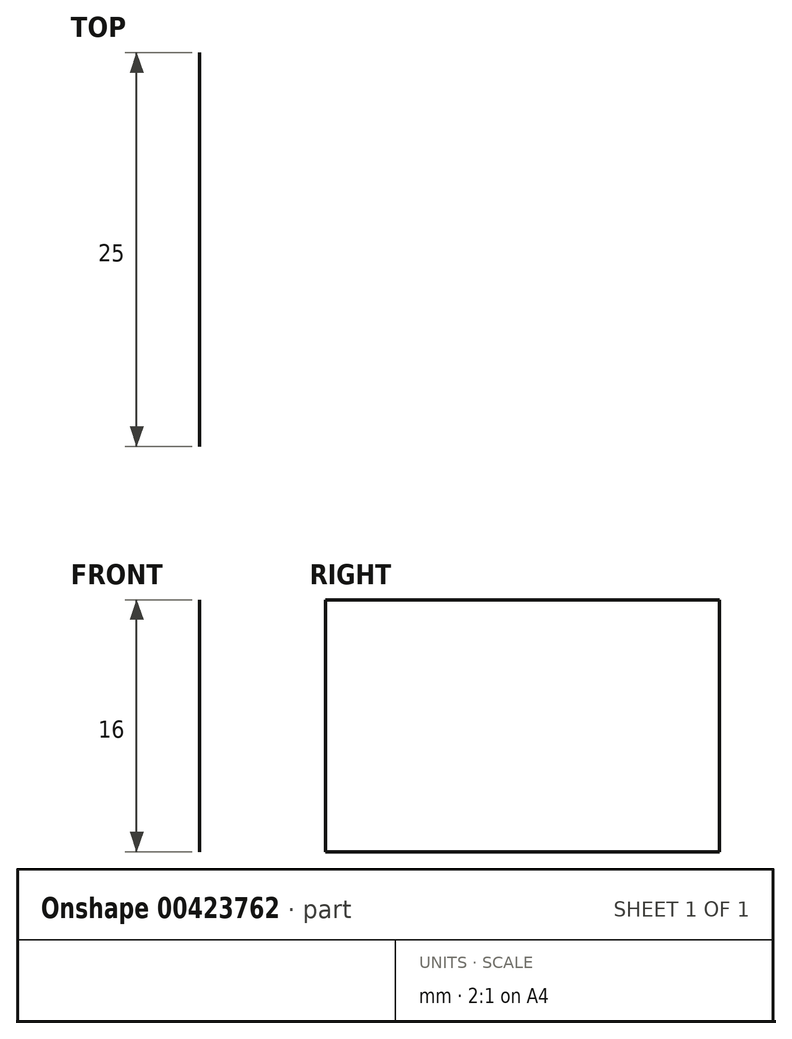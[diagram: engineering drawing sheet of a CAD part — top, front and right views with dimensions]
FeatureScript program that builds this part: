
annotation { "Feature Type Name" : "Feature", "Feature Type Description" : "" }
export const myFeature = defineFeature(function(context is Context, id is Id, definition is map)
    precondition{}
    {
        {
            var Q0;
            Q0=qCreatedBy(makeId("Front.planeOp"),FACE);
            var sketch = newSketch(context, id + "F0", { "sketchPlane" : qUnion([Q0])});
            skLineSegment(sketch, "E0", {"start": v(0, 0) * mm, "end": v(16, 0) * mm});
            skLineSegment(sketch, "E1", {"start": v(-16, 0) * mm, "end": v(0, 0) * mm});
            skLineSegment(sketch, "E2", {"start": v(-16, 0) * mm, "end": v(-16, 16) * mm});
            skLineSegment(sketch, "E3", {"start": v(-16, 0) * mm, "end": v(-16, -16) * mm});
            skLineSegment(sketch, "E4", {"start": v(16, 0) * mm, "end": v(16, 16) * mm});
            skLineSegment(sketch, "E5", {"start": v(16, 0) * mm, "end": v(16, -16) * mm});
            skSolve(sketch);
        }
        {
            var Q0;
            Q0=sQuery(id+"F0.wireOp",EDGE,"E2");
            extrude(context, id + "F1", {"bodyType" : ToolBodyType.SURFACE, "surfaceEntities" : qUnion([Q0]), "depth" : 25 * mm});
        }
    });
